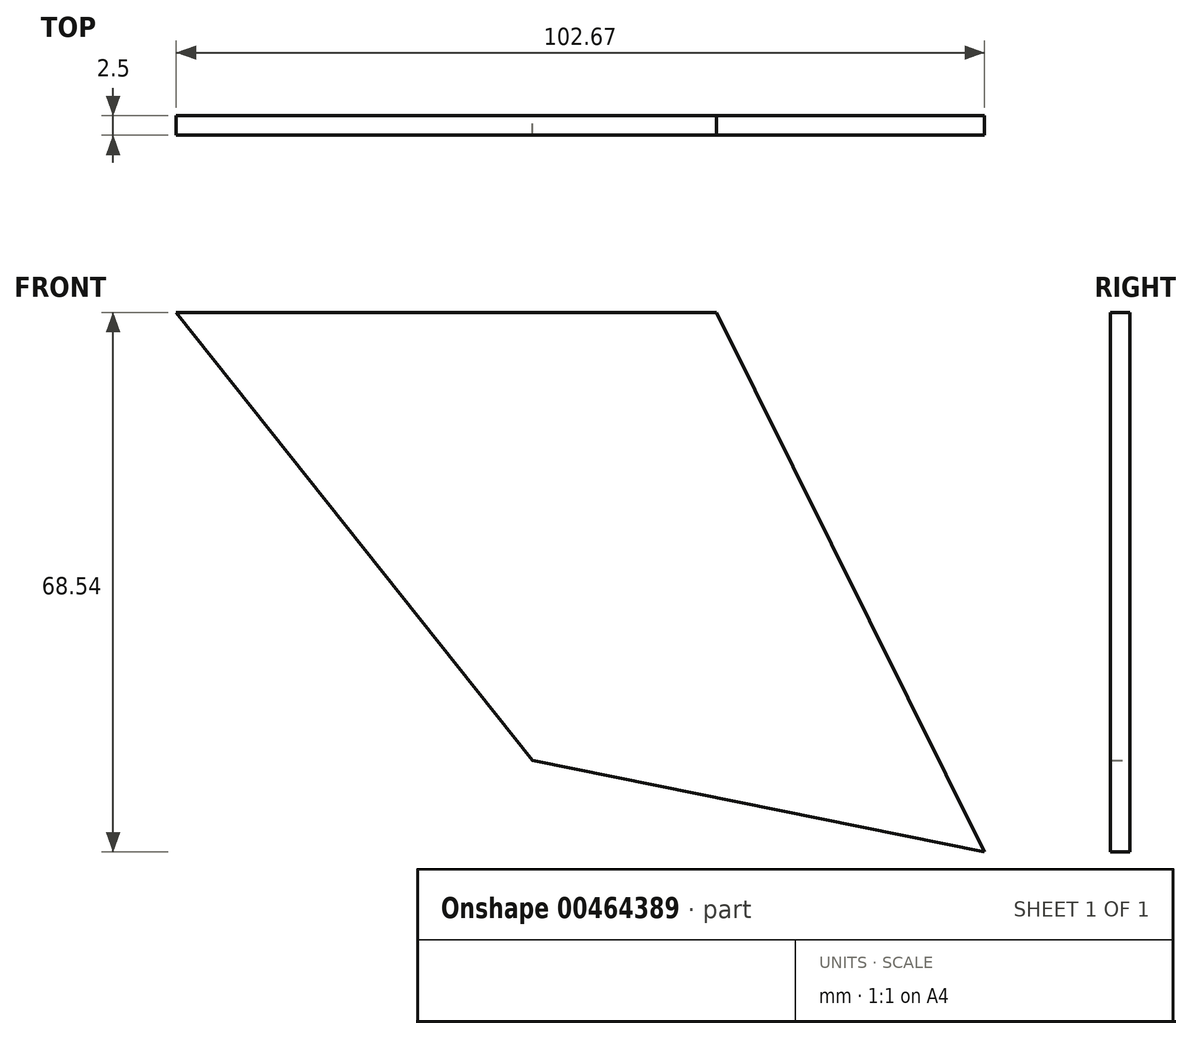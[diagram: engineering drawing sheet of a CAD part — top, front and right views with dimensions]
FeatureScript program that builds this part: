
annotation { "Feature Type Name" : "Feature", "Feature Type Description" : "" }
export const myFeature = defineFeature(function(context is Context, id is Id, definition is map)
    precondition{}
    {
        {
            var Q0;
            Q0=qCreatedBy(makeId("Front.planeOp"),FACE);
            var sketch = newSketch(context, id + "F0", { "sketchPlane" : qUnion([Q0])});
            skLineSegment(sketch, "E0", {"start": v(-55.34, 39.96) * mm, "end": v(-10.09, -16.94) * mm});
            skLineSegment(sketch, "E1", {"start": v(-10.09, -16.94) * mm, "end": v(47.33, -28.58) * mm});
            skLineSegment(sketch, "E2", {"start": v(-55.34, 39.96) * mm, "end": v(13.29, 39.96) * mm});
            skLineSegment(sketch, "E3", {"start": v(13.29, 39.96) * mm, "end": v(47.33, -28.58) * mm});
            skSolve(sketch);
        }
        {
            var Q0;
            Q0=makeQuery(id+"F0.imprint","IMPRINT",FACE,{"disambiguationData":[TD([[makeQuery(id+"F0.imprint","IMPRINT",EDGE,{"derivedFrom":sQuery(id+"F0.wireOp",EDGE,"E0")}),1.0]])]});
            extrude(context, id + "F1", {"entities" : qUnion([Q0]), "depth" : 2.5 * mm});
        }
    });
